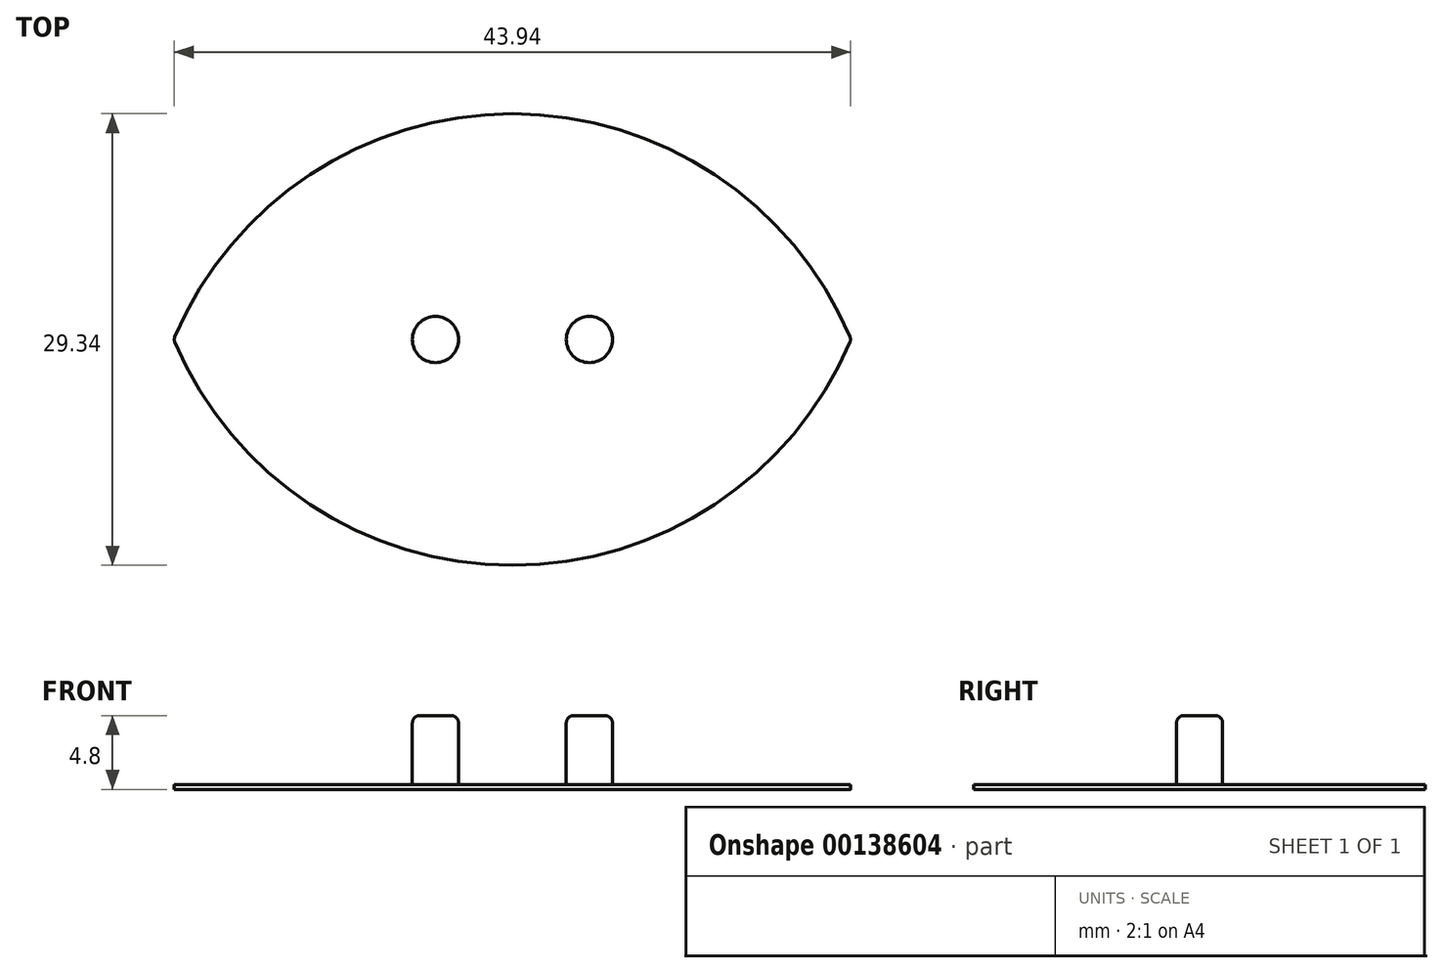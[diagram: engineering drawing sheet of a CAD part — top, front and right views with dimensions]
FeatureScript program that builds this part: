
annotation { "Feature Type Name" : "Feature", "Feature Type Description" : "" }
export const myFeature = defineFeature(function(context is Context, id is Id, definition is map)
    precondition{}
    {
        {
            assignVariable(context, id + "F0", {"name" : "pin_end_fillet", "anyValue" : 0.5 * mm});
        }
        {
            assignVariable(context, id + "F1", {"name" : "pin_length", "anyValue" : 4.5 * mm});
        }
        {
            var Q0;
            Q0=qCreatedBy(makeId("Top.planeOp"),FACE);
            var sketch = newSketch(context, id + "F2", { "sketchPlane" : qUnion([Q0])});
            skCircle(sketch, "E0", {"center": v(0, 0) * mm, "radius": 22 * mm, "construction": true});
            skLineSegment(sketch, "E1", {"start": v(-22, 0) * mm, "end": v(22, 0) * mm, "construction": true});
            skLineSegment(sketch, "E2", {"start": v(0, 22) * mm, "end": v(0, 14.67) * mm, "construction": true});
            skLineSegment(sketch, "E3", {"start": v(0, 14.67) * mm, "end": v(0, 7.33) * mm, "construction": true});
            skLineSegment(sketch, "E4", {"start": v(0, 7.33) * mm, "end": v(0, 0) * mm, "construction": true});
            skArc(sketch, "E5", {"start": v(21.93, 0.16) * mm, "mid": v(0, 14.67) * mm, "end": v(-21.93, 0.16) * mm});
            skArc(sketch, "E6.MirrorCS", {"start": v(21.93, -0.16) * mm, "mid": v(0, -14.67) * mm, "end": v(-21.93, -0.16) * mm});
            skPoint(sketch, "E7.visualSharp", {"position": v(22, 0) * mm});
            skArc(sketch, "E7.filletArc", {"start": v(21.93, -0.16) * mm, "mid": v(21.97, 0) * mm, "end": v(21.93, 0.16) * mm});
            skPoint(sketch, "E8.visualSharp", {"position": v(-22, 0) * mm});
            skArc(sketch, "E8.filletArc", {"start": v(-21.93, 0.16) * mm, "mid": v(-21.97, 0) * mm, "end": v(-21.93, -0.16) * mm});
            skSolve(sketch);
        }
        {
            var Q0;
            Q0=makeQuery(id+"F2.imprint","IMPRINT",FACE,{"disambiguationData":[TD([[makeQuery(id+"F2.imprint","IMPRINT",EDGE,{"derivedFrom":sQuery(id+"F2.wireOp",EDGE,"E5")}),1.0]])]});
            extrude(context, id + "F3", {"entities" : qUnion([Q0]), "depth" : 0.3 * mm});
        }
        {
            var Q0;
            Q0=makeQuery(id+"F3.opExtrude","CAP_FACE",FACE,{"disambiguationData":[OSD([sQuery(id+"F2.wireOp",EDGE,"E5"),sQuery(id+"F2.wireOp",EDGE,"E6.MirrorCS"),sQuery(id+"F2.wireOp",EDGE,"E7.filletArc"),sQuery(id+"F2.wireOp",EDGE,"E8.filletArc")])],"isStart":false});
            var sketch = newSketch(context, id + "F4", { "sketchPlane" : qUnion([Q0])});
            skLineSegment(sketch, "E9", {"start": v(0, 0) * mm, "end": v(5, 0) * mm, "construction": true});
            skLineSegment(sketch, "E10", {"start": v(0, 0) * mm, "end": v(-5, 0) * mm, "construction": true});
            skCircle(sketch, "E11", {"center": v(5, 0) * mm, "radius": 1.5 * mm});
            skCircle(sketch, "E12", {"center": v(-5, 0) * mm, "radius": 1.5 * mm});
            skSolve(sketch);
        }
        {
            var Q0;
            Q0=makeQuery(id+"F4.imprint","IMPRINT",FACE,{"disambiguationData":[TD([[makeQuery(id+"F4.imprint","IMPRINT",EDGE,{"derivedFrom":sQuery(id+"F4.wireOp",EDGE,"E12")}),1.0]])]});
            var Q1;
            Q1=makeQuery(id+"F4.imprint","IMPRINT",FACE,{"disambiguationData":[TD([[makeQuery(id+"F4.imprint","IMPRINT",EDGE,{"derivedFrom":sQuery(id+"F4.wireOp",EDGE,"E11")}),1.0]])]});
            extrude(context, id + "F5", {"entities" : qUnion([Q0, Q1]), "operationType" : NewBodyOperationType.ADD, "depth" : getVariable(context, 'pin_length')});
        }
        {
            var Q0;
            Q0=makeQuery(id+"F5.opExtrude","CAP_EDGE",EDGE,{"disambiguationData":[OSD([sQuery(id+"F4.wireOp",EDGE,"E12")])],"isStart":false});
            var Q1;
            Q1=makeQuery(id+"F5.opExtrude","CAP_EDGE",EDGE,{"disambiguationData":[OSD([sQuery(id+"F4.wireOp",EDGE,"E11")])],"isStart":false});
            fillet(context, id + "F6", {"entities" : qUnion([Q0, Q1]), "radius" : getVariable(context, 'pin_end_fillet'), "tangentPropagation" : true, "allowEdgeOverflow" : false});
        }
    });
